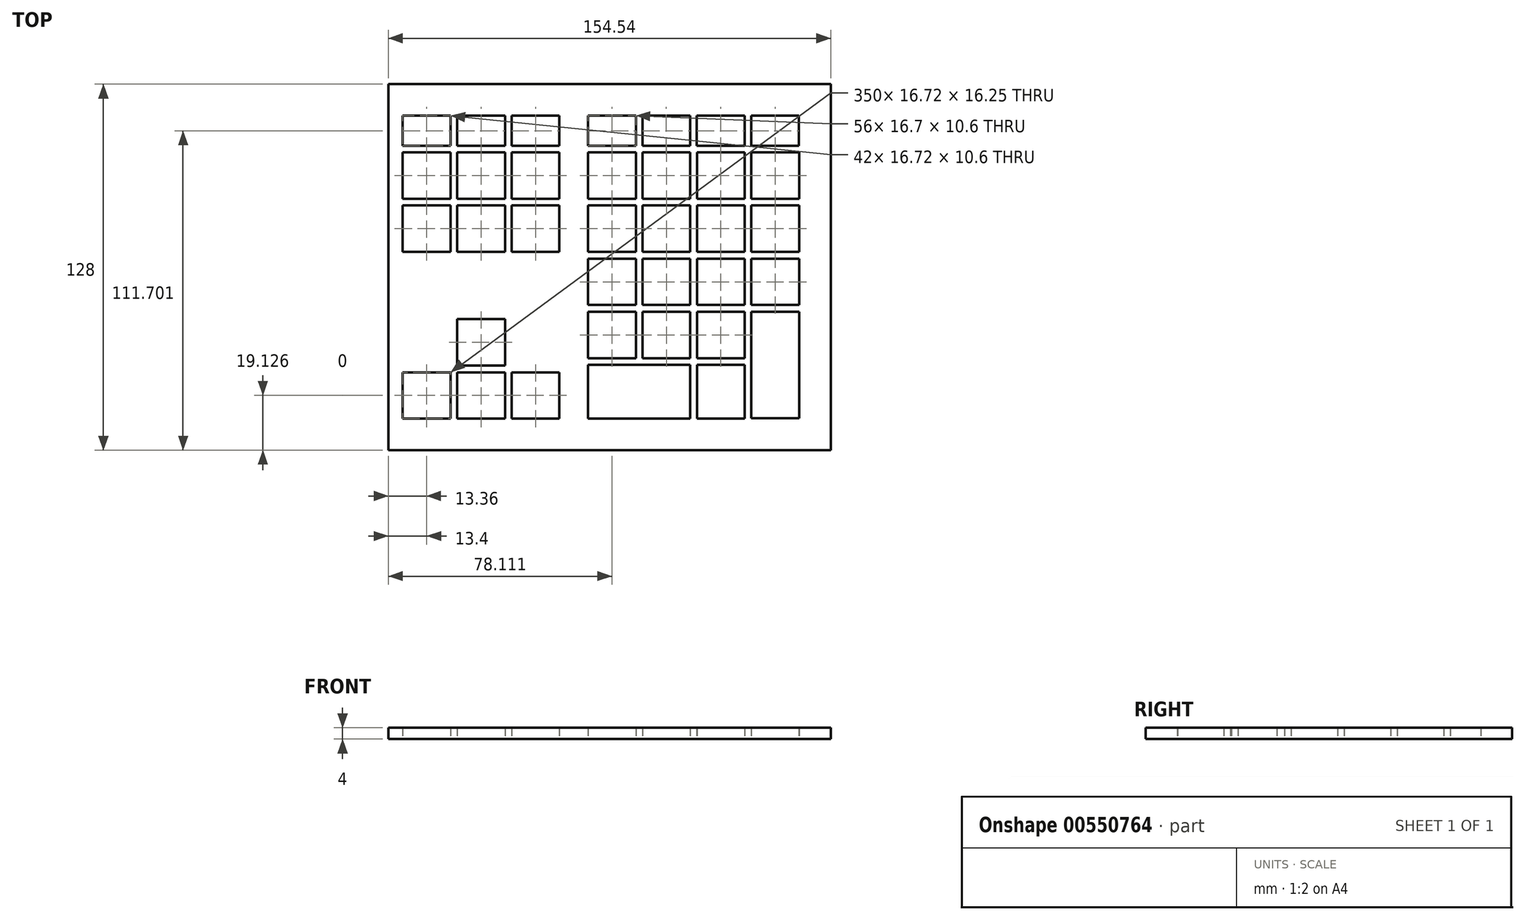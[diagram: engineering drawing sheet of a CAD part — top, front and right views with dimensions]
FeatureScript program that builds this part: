
annotation { "Feature Type Name" : "Feature", "Feature Type Description" : "" }
export const myFeature = defineFeature(function(context is Context, id is Id, definition is map)
    precondition{}
    {
        {
            var Q0;
            Q0=qCreatedBy(makeId("Top.planeOp"),FACE);
            var sketch = newSketch(context, id + "F0", { "sketchPlane" : qUnion([Q0])});
            skLineSegment(sketch, "E0.right", {"start": v(19.3, 78.42) * mm, "end": v(19.3, -35.58) * mm, "construction": true});
            skLineSegment(sketch, "E1.bottom", {"start": v(-123.2, 74.42) * mm, "end": v(-106.49, 74.42) * mm});
            skLineSegment(sketch, "E1.top", {"start": v(-123.2, 63.82) * mm, "end": v(-106.49, 63.82) * mm});
            skLineSegment(sketch, "E1.left", {"start": v(-123.2, 74.42) * mm, "end": v(-123.2, 63.82) * mm});
            skLineSegment(sketch, "E1.right", {"start": v(-106.49, 74.42) * mm, "end": v(-106.49, 63.82) * mm});
            skPoint(sketch, "E1.middle", {"position": v(-114.85, 69.12) * mm});
            skLineSegment(sketch, "E2.1.0.0", {"start": v(-87.49, 74.42) * mm, "end": v(-87.49, 63.82) * mm});
            skLineSegment(sketch, "E2.1.0.1", {"start": v(-104.2, 74.42) * mm, "end": v(-104.2, 63.82) * mm});
            skLineSegment(sketch, "E2.1.0.2", {"start": v(-104.2, 74.42) * mm, "end": v(-87.49, 74.42) * mm});
            skPoint(sketch, "E2.1.0.3", {"position": v(-95.85, 69.12) * mm});
            skLineSegment(sketch, "E2.1.0.4", {"start": v(-104.2, 63.82) * mm, "end": v(-87.49, 63.82) * mm});
            skLineSegment(sketch, "E2.2.0.0", {"start": v(-68.49, 74.42) * mm, "end": v(-68.49, 63.82) * mm});
            skLineSegment(sketch, "E2.2.0.1", {"start": v(-85.2, 74.42) * mm, "end": v(-85.2, 63.82) * mm});
            skLineSegment(sketch, "E2.2.0.2", {"start": v(-85.2, 74.42) * mm, "end": v(-68.49, 74.42) * mm});
            skPoint(sketch, "E2.2.0.3", {"position": v(-76.85, 69.12) * mm});
            skLineSegment(sketch, "E2.2.0.4", {"start": v(-85.2, 63.82) * mm, "end": v(-68.49, 63.82) * mm});
            skLineSegment(sketch, "E3.bottom", {"start": v(-58.49, 74.42) * mm, "end": v(-41.79, 74.42) * mm});
            skLineSegment(sketch, "E3.top", {"start": v(-58.49, 63.82) * mm, "end": v(-41.79, 63.82) * mm});
            skLineSegment(sketch, "E3.left", {"start": v(-58.49, 74.42) * mm, "end": v(-58.49, 63.82) * mm});
            skLineSegment(sketch, "E3.right", {"start": v(-41.79, 74.42) * mm, "end": v(-41.79, 63.82) * mm});
            skPoint(sketch, "E3.middle", {"position": v(-50.14, 69.12) * mm});
            skLineSegment(sketch, "E4.1.0.0", {"start": v(-22.79, 74.42) * mm, "end": v(-22.79, 63.82) * mm});
            skLineSegment(sketch, "E4.1.0.1", {"start": v(-39.49, 74.42) * mm, "end": v(-22.79, 74.42) * mm});
            skLineSegment(sketch, "E4.1.0.2", {"start": v(-39.49, 63.82) * mm, "end": v(-22.79, 63.82) * mm});
            skLineSegment(sketch, "E4.1.0.3", {"start": v(-39.49, 74.42) * mm, "end": v(-39.49, 63.82) * mm});
            skPoint(sketch, "E4.1.0.4", {"position": v(-31.14, 69.12) * mm});
            skLineSegment(sketch, "E4.2.0.0", {"start": v(-3.79, 74.42) * mm, "end": v(-3.79, 63.82) * mm});
            skLineSegment(sketch, "E4.2.0.1", {"start": v(-20.49, 74.42) * mm, "end": v(-3.79, 74.42) * mm});
            skLineSegment(sketch, "E4.2.0.2", {"start": v(-20.49, 63.82) * mm, "end": v(-3.79, 63.82) * mm});
            skLineSegment(sketch, "E4.2.0.3", {"start": v(-20.49, 74.42) * mm, "end": v(-20.49, 63.82) * mm});
            skPoint(sketch, "E4.2.0.4", {"position": v(-12.14, 69.12) * mm});
            skLineSegment(sketch, "E4.3.0.0", {"start": v(15.21, 74.42) * mm, "end": v(15.21, 63.82) * mm});
            skLineSegment(sketch, "E4.3.0.1", {"start": v(-1.49, 74.42) * mm, "end": v(15.21, 74.42) * mm});
            skLineSegment(sketch, "E4.3.0.2", {"start": v(-1.49, 63.82) * mm, "end": v(15.21, 63.82) * mm});
            skLineSegment(sketch, "E4.3.0.3", {"start": v(-1.49, 74.42) * mm, "end": v(-1.49, 63.82) * mm});
            skPoint(sketch, "E4.3.0.4", {"position": v(6.86, 69.12) * mm});
            skLineSegment(sketch, "E5.bottom", {"start": v(-123.25, 61.52) * mm, "end": v(-106.53, 61.52) * mm});
            skLineSegment(sketch, "E5.top", {"start": v(-123.25, 45.27) * mm, "end": v(-106.53, 45.27) * mm});
            skLineSegment(sketch, "E5.left", {"start": v(-123.25, 61.52) * mm, "end": v(-123.25, 45.27) * mm});
            skLineSegment(sketch, "E5.right", {"start": v(-106.53, 61.52) * mm, "end": v(-106.53, 45.27) * mm});
            skPoint(sketch, "E5.middle", {"position": v(-114.89, 53.4) * mm});
            skPoint(sketch, "E6.1.0.0", {"position": v(-95.87, 53.4) * mm});
            skLineSegment(sketch, "E6.1.0.1", {"start": v(-104.23, 45.27) * mm, "end": v(-87.5, 45.27) * mm});
            skLineSegment(sketch, "E6.1.0.2", {"start": v(-87.5, 61.52) * mm, "end": v(-87.5, 45.27) * mm});
            skLineSegment(sketch, "E6.1.0.3", {"start": v(-104.23, 61.52) * mm, "end": v(-87.5, 61.52) * mm});
            skLineSegment(sketch, "E6.1.0.4", {"start": v(-104.23, 61.52) * mm, "end": v(-104.23, 45.27) * mm});
            skPoint(sketch, "E6.2.0.0", {"position": v(-76.85, 53.4) * mm});
            skLineSegment(sketch, "E6.2.0.1", {"start": v(-85.2, 45.27) * mm, "end": v(-68.49, 45.27) * mm});
            skLineSegment(sketch, "E6.2.0.2", {"start": v(-68.49, 61.52) * mm, "end": v(-68.49, 45.27) * mm});
            skLineSegment(sketch, "E6.2.0.3", {"start": v(-85.2, 61.52) * mm, "end": v(-68.49, 61.52) * mm});
            skLineSegment(sketch, "E6.2.0.4", {"start": v(-85.2, 61.52) * mm, "end": v(-85.2, 45.27) * mm});
            skLineSegment(sketch, "E7.bottom", {"start": v(-123.25, 42.97) * mm, "end": v(-106.53, 42.97) * mm});
            skLineSegment(sketch, "E7.top", {"start": v(-123.25, 26.72) * mm, "end": v(-106.53, 26.72) * mm});
            skLineSegment(sketch, "E7.left", {"start": v(-123.25, 42.97) * mm, "end": v(-123.25, 26.72) * mm});
            skLineSegment(sketch, "E7.right", {"start": v(-106.53, 42.97) * mm, "end": v(-106.53, 26.72) * mm});
            skPoint(sketch, "E7.middle", {"position": v(-114.89, 34.85) * mm});
            skLineSegment(sketch, "E8.1.0.0", {"start": v(-104.23, 26.72) * mm, "end": v(-87.5, 26.72) * mm});
            skLineSegment(sketch, "E8.1.0.1", {"start": v(-104.23, 42.97) * mm, "end": v(-87.5, 42.97) * mm});
            skLineSegment(sketch, "E8.1.0.2", {"start": v(-104.23, 42.97) * mm, "end": v(-104.23, 26.72) * mm});
            skPoint(sketch, "E8.1.0.3", {"position": v(-95.87, 34.85) * mm});
            skLineSegment(sketch, "E8.1.0.4", {"start": v(-87.5, 42.97) * mm, "end": v(-87.5, 26.72) * mm});
            skLineSegment(sketch, "E8.2.0.0", {"start": v(-85.2, 26.72) * mm, "end": v(-68.49, 26.72) * mm});
            skLineSegment(sketch, "E8.2.0.1", {"start": v(-85.2, 42.97) * mm, "end": v(-68.49, 42.97) * mm});
            skLineSegment(sketch, "E8.2.0.2", {"start": v(-85.2, 42.97) * mm, "end": v(-85.2, 26.72) * mm});
            skPoint(sketch, "E8.2.0.3", {"position": v(-76.85, 34.85) * mm});
            skLineSegment(sketch, "E8.2.0.4", {"start": v(-68.49, 42.97) * mm, "end": v(-68.49, 26.72) * mm});
            skPoint(sketch, "E9.1.0.0", {"position": v(-50.13, 53.4) * mm});
            skLineSegment(sketch, "E9.1.0.1", {"start": v(-58.49, 61.52) * mm, "end": v(-41.77, 61.52) * mm});
            skLineSegment(sketch, "E9.1.0.3", {"start": v(-41.77, 61.52) * mm, "end": v(-41.77, 45.27) * mm});
            skLineSegment(sketch, "E9.1.0.4", {"start": v(-58.49, 45.27) * mm, "end": v(-41.77, 45.27) * mm});
            skLineSegment(sketch, "E9.1.0.7", {"start": v(-58.49, 61.52) * mm, "end": v(-58.49, 45.27) * mm});
            skLineSegment(sketch, "E10.0.1.0", {"start": v(-58.49, 42.97) * mm, "end": v(-58.49, 26.72) * mm});
            skPoint(sketch, "E10.0.1.1", {"position": v(-50.13, 34.85) * mm});
            skLineSegment(sketch, "E10.0.1.2", {"start": v(-58.49, 42.97) * mm, "end": v(-41.77, 42.97) * mm});
            skLineSegment(sketch, "E10.0.1.3", {"start": v(-41.77, 42.97) * mm, "end": v(-41.77, 26.72) * mm});
            skLineSegment(sketch, "E10.0.1.4", {"start": v(-58.49, 26.72) * mm, "end": v(-41.77, 26.72) * mm});
            skLineSegment(sketch, "E10.0.2.0", {"start": v(-58.49, 24.42) * mm, "end": v(-58.49, 8.17) * mm});
            skPoint(sketch, "E10.0.2.1", {"position": v(-50.13, 16.3) * mm});
            skLineSegment(sketch, "E10.0.2.2", {"start": v(-58.49, 24.42) * mm, "end": v(-41.77, 24.42) * mm});
            skLineSegment(sketch, "E10.0.2.3", {"start": v(-41.77, 24.42) * mm, "end": v(-41.77, 8.17) * mm});
            skLineSegment(sketch, "E10.0.2.4", {"start": v(-58.49, 8.17) * mm, "end": v(-41.77, 8.17) * mm});
            skLineSegment(sketch, "E10.0.3.0", {"start": v(-58.49, 5.87) * mm, "end": v(-58.49, -10.38) * mm});
            skPoint(sketch, "E10.0.3.1", {"position": v(-50.13, -2.25) * mm});
            skLineSegment(sketch, "E10.0.3.2", {"start": v(-58.49, 5.87) * mm, "end": v(-41.77, 5.87) * mm});
            skLineSegment(sketch, "E10.0.3.3", {"start": v(-41.77, 5.87) * mm, "end": v(-41.77, -10.38) * mm});
            skLineSegment(sketch, "E10.0.3.4", {"start": v(-58.49, -10.38) * mm, "end": v(-41.77, -10.38) * mm});
            skLineSegment(sketch, "E10.1.0.0", {"start": v(-39.47, 61.52) * mm, "end": v(-39.47, 45.27) * mm});
            skPoint(sketch, "E10.1.0.1", {"position": v(-31.1, 53.4) * mm});
            skLineSegment(sketch, "E10.1.0.2", {"start": v(-39.47, 61.52) * mm, "end": v(-22.75, 61.52) * mm});
            skLineSegment(sketch, "E10.1.0.3", {"start": v(-22.75, 61.52) * mm, "end": v(-22.75, 45.27) * mm});
            skLineSegment(sketch, "E10.1.0.4", {"start": v(-39.47, 45.27) * mm, "end": v(-22.75, 45.27) * mm});
            skLineSegment(sketch, "E10.1.1.0", {"start": v(-39.47, 42.97) * mm, "end": v(-39.47, 26.72) * mm});
            skPoint(sketch, "E10.1.1.1", {"position": v(-31.1, 34.85) * mm});
            skLineSegment(sketch, "E10.1.1.2", {"start": v(-39.47, 42.97) * mm, "end": v(-22.75, 42.97) * mm});
            skLineSegment(sketch, "E10.1.1.3", {"start": v(-22.75, 42.97) * mm, "end": v(-22.75, 26.72) * mm});
            skLineSegment(sketch, "E10.1.1.4", {"start": v(-39.47, 26.72) * mm, "end": v(-22.75, 26.72) * mm});
            skLineSegment(sketch, "E10.1.2.0", {"start": v(-39.47, 24.42) * mm, "end": v(-39.47, 8.17) * mm});
            skPoint(sketch, "E10.1.2.1", {"position": v(-31.1, 16.3) * mm});
            skLineSegment(sketch, "E10.1.2.2", {"start": v(-39.47, 24.42) * mm, "end": v(-22.75, 24.42) * mm});
            skLineSegment(sketch, "E10.1.2.3", {"start": v(-22.75, 24.42) * mm, "end": v(-22.75, 8.17) * mm});
            skLineSegment(sketch, "E10.1.2.4", {"start": v(-39.47, 8.17) * mm, "end": v(-22.75, 8.17) * mm});
            skLineSegment(sketch, "E10.1.3.0", {"start": v(-39.47, 5.87) * mm, "end": v(-39.47, -10.38) * mm});
            skPoint(sketch, "E10.1.3.1", {"position": v(-31.1, -2.25) * mm});
            skLineSegment(sketch, "E10.1.3.2", {"start": v(-39.47, 5.87) * mm, "end": v(-22.75, 5.87) * mm});
            skLineSegment(sketch, "E10.1.3.3", {"start": v(-22.75, 5.87) * mm, "end": v(-22.75, -10.38) * mm});
            skLineSegment(sketch, "E10.1.3.4", {"start": v(-39.47, -10.38) * mm, "end": v(-22.75, -10.38) * mm});
            skLineSegment(sketch, "E10.2.0.0", {"start": v(-20.45, 61.52) * mm, "end": v(-20.45, 45.27) * mm});
            skPoint(sketch, "E10.2.0.1", {"position": v(-12.09, 53.4) * mm});
            skLineSegment(sketch, "E10.2.0.2", {"start": v(-20.45, 61.52) * mm, "end": v(-3.73, 61.52) * mm});
            skLineSegment(sketch, "E10.2.0.3", {"start": v(-3.73, 61.52) * mm, "end": v(-3.73, 45.27) * mm});
            skLineSegment(sketch, "E10.2.0.4", {"start": v(-20.45, 45.27) * mm, "end": v(-3.73, 45.27) * mm});
            skLineSegment(sketch, "E10.2.1.0", {"start": v(-20.45, 42.97) * mm, "end": v(-20.45, 26.72) * mm});
            skPoint(sketch, "E10.2.1.1", {"position": v(-12.09, 34.85) * mm});
            skLineSegment(sketch, "E10.2.1.2", {"start": v(-20.45, 42.97) * mm, "end": v(-3.73, 42.97) * mm});
            skLineSegment(sketch, "E10.2.1.3", {"start": v(-3.73, 42.97) * mm, "end": v(-3.73, 26.72) * mm});
            skLineSegment(sketch, "E10.2.1.4", {"start": v(-20.45, 26.72) * mm, "end": v(-3.73, 26.72) * mm});
            skLineSegment(sketch, "E10.2.2.0", {"start": v(-20.45, 24.42) * mm, "end": v(-20.45, 8.17) * mm});
            skPoint(sketch, "E10.2.2.1", {"position": v(-12.09, 16.3) * mm});
            skLineSegment(sketch, "E10.2.2.2", {"start": v(-20.45, 24.42) * mm, "end": v(-3.73, 24.42) * mm});
            skLineSegment(sketch, "E10.2.2.3", {"start": v(-3.73, 24.42) * mm, "end": v(-3.73, 8.17) * mm});
            skLineSegment(sketch, "E10.2.2.4", {"start": v(-20.45, 8.17) * mm, "end": v(-3.73, 8.17) * mm});
            skLineSegment(sketch, "E10.2.3.0", {"start": v(-20.45, 5.87) * mm, "end": v(-20.45, -10.38) * mm});
            skPoint(sketch, "E10.2.3.1", {"position": v(-12.09, -2.25) * mm});
            skLineSegment(sketch, "E10.2.3.2", {"start": v(-20.45, 5.87) * mm, "end": v(-3.73, 5.87) * mm});
            skLineSegment(sketch, "E10.2.3.3", {"start": v(-3.73, 5.87) * mm, "end": v(-3.73, -10.38) * mm});
            skLineSegment(sketch, "E10.2.3.4", {"start": v(-20.45, -10.38) * mm, "end": v(-3.73, -10.38) * mm});
            skLineSegment(sketch, "E10.3.0.0", {"start": v(-1.43, 61.52) * mm, "end": v(-1.43, 45.27) * mm});
            skPoint(sketch, "E10.3.0.1", {"position": v(6.93, 53.4) * mm});
            skLineSegment(sketch, "E10.3.0.2", {"start": v(-1.43, 61.52) * mm, "end": v(15.3, 61.52) * mm});
            skLineSegment(sketch, "E10.3.0.3", {"start": v(15.3, 61.52) * mm, "end": v(15.3, 45.27) * mm});
            skLineSegment(sketch, "E10.3.0.4", {"start": v(-1.43, 45.27) * mm, "end": v(15.3, 45.27) * mm});
            skLineSegment(sketch, "E10.3.1.0", {"start": v(-1.43, 42.97) * mm, "end": v(-1.43, 26.72) * mm});
            skPoint(sketch, "E10.3.1.1", {"position": v(6.93, 34.85) * mm});
            skLineSegment(sketch, "E10.3.1.2", {"start": v(-1.43, 42.97) * mm, "end": v(15.3, 42.97) * mm});
            skLineSegment(sketch, "E10.3.1.3", {"start": v(15.3, 42.97) * mm, "end": v(15.3, 26.72) * mm});
            skLineSegment(sketch, "E10.3.1.4", {"start": v(-1.43, 26.72) * mm, "end": v(15.3, 26.72) * mm});
            skLineSegment(sketch, "E10.3.2.0", {"start": v(-1.43, 24.42) * mm, "end": v(-1.43, 8.17) * mm});
            skPoint(sketch, "E10.3.2.1", {"position": v(6.93, 16.3) * mm});
            skLineSegment(sketch, "E10.3.2.2", {"start": v(-1.43, 24.42) * mm, "end": v(15.3, 24.42) * mm});
            skLineSegment(sketch, "E10.3.2.3", {"start": v(15.3, 24.42) * mm, "end": v(15.3, 8.17) * mm});
            skLineSegment(sketch, "E10.3.2.4", {"start": v(-1.43, 8.17) * mm, "end": v(15.3, 8.17) * mm});
            skLineSegment(sketch, "E10.3.3.0", {"start": v(-1.43, 5.87) * mm, "end": v(-1.43, -31.43) * mm});
            skPoint(sketch, "E10.3.3.1", {"position": v(6.93, -12.78) * mm});
            skLineSegment(sketch, "E10.3.3.2", {"start": v(-1.43, 5.87) * mm, "end": v(15.3, 5.87) * mm});
            skLineSegment(sketch, "E10.3.3.3", {"start": v(15.3, 5.87) * mm, "end": v(15.3, -31.43) * mm});
            skLineSegment(sketch, "E10.3.3.4", {"start": v(-1.43, -31.43) * mm, "end": v(15.3, -31.43) * mm});
            skLineSegment(sketch, "E11.bottom", {"start": v(-20.45, -12.68) * mm, "end": v(-3.73, -12.68) * mm});
            skLineSegment(sketch, "E11.top", {"start": v(-20.45, -31.49) * mm, "end": v(-3.73, -31.49) * mm});
            skLineSegment(sketch, "E11.left", {"start": v(-20.45, -12.68) * mm, "end": v(-20.45, -31.49) * mm});
            skLineSegment(sketch, "E11.right", {"start": v(-3.73, -12.68) * mm, "end": v(-3.73, -31.49) * mm});
            skPoint(sketch, "E11.middle", {"position": v(-12.09, -22.08) * mm});
            skLineSegment(sketch, "E12.bottom", {"start": v(-58.49, -12.68) * mm, "end": v(-22.75, -12.68) * mm});
            skLineSegment(sketch, "E12.top", {"start": v(-58.49, -31.49) * mm, "end": v(-22.75, -31.49) * mm});
            skLineSegment(sketch, "E12.left", {"start": v(-58.49, -12.68) * mm, "end": v(-58.49, -31.49) * mm});
            skLineSegment(sketch, "E12.right", {"start": v(-22.75, -12.68) * mm, "end": v(-22.75, -31.49) * mm});
            skPoint(sketch, "E12.middle", {"position": v(-40.62, -22.08) * mm});
            skLineSegment(sketch, "E13.bottom", {"start": v(-85.2, -15.33) * mm, "end": v(-68.49, -15.33) * mm});
            skLineSegment(sketch, "E13.top", {"start": v(-85.2, -31.58) * mm, "end": v(-68.49, -31.58) * mm});
            skLineSegment(sketch, "E13.left", {"start": v(-85.2, -15.33) * mm, "end": v(-85.2, -31.58) * mm});
            skLineSegment(sketch, "E13.right", {"start": v(-68.49, -15.33) * mm, "end": v(-68.49, -31.58) * mm});
            skPoint(sketch, "E13.middle", {"position": v(-76.85, -23.45) * mm});
            skPoint(sketch, "E14.1.0.0", {"position": v(-95.87, -23.45) * mm});
            skLineSegment(sketch, "E14.1.0.1", {"start": v(-104.23, -31.58) * mm, "end": v(-87.5, -31.58) * mm});
            skLineSegment(sketch, "E14.1.0.2", {"start": v(-104.23, -15.33) * mm, "end": v(-87.5, -15.33) * mm});
            skLineSegment(sketch, "E14.1.0.3", {"start": v(-87.5, -15.33) * mm, "end": v(-87.5, -31.58) * mm});
            skLineSegment(sketch, "E14.1.0.4", {"start": v(-104.23, -15.33) * mm, "end": v(-104.23, -31.58) * mm});
            skPoint(sketch, "E14.2.0.0", {"position": v(-114.89, -23.45) * mm});
            skLineSegment(sketch, "E14.2.0.1", {"start": v(-123.25, -31.58) * mm, "end": v(-106.53, -31.58) * mm});
            skLineSegment(sketch, "E14.2.0.2", {"start": v(-123.25, -15.33) * mm, "end": v(-106.53, -15.33) * mm});
            skLineSegment(sketch, "E14.2.0.3", {"start": v(-106.53, -15.33) * mm, "end": v(-106.53, -31.58) * mm});
            skLineSegment(sketch, "E14.2.0.4", {"start": v(-123.25, -15.33) * mm, "end": v(-123.25, -31.58) * mm});
            skLineSegment(sketch, "E15.0.1.0", {"start": v(-104.23, 3.22) * mm, "end": v(-87.5, 3.22) * mm});
            skLineSegment(sketch, "E15.0.1.1", {"start": v(-104.23, 3.22) * mm, "end": v(-104.23, -13.03) * mm});
            skLineSegment(sketch, "E15.0.1.2", {"start": v(-87.5, 3.22) * mm, "end": v(-87.5, -13.03) * mm});
            skPoint(sketch, "E15.0.1.3", {"position": v(-95.87, -4.9) * mm});
            skLineSegment(sketch, "E15.0.1.4", {"start": v(-104.23, -13.03) * mm, "end": v(-87.5, -13.03) * mm});
            skLineSegment(sketch, "E16.right", {"start": v(26.3, 85.42) * mm, "end": v(26.3, -42.58) * mm});
            skLineSegment(sketch, "E17", {"start": v(-128.25, 85.42) * mm, "end": v(-128.25, 78.42) * mm});
            skLineSegment(sketch, "E18", {"start": v(-128.25, 85.42) * mm, "end": v(26.3, 85.42) * mm});
            skLineSegment(sketch, "E19", {"start": v(-128.25, -42.58) * mm, "end": v(26.3, -42.58) * mm});
            skLineSegment(sketch, "E20", {"start": v(-128.25, -35.58) * mm, "end": v(-128.25, -42.58) * mm});
            skLineSegment(sketch, "E21", {"start": v(-128.25, 78.42) * mm, "end": v(-128.25, -35.58) * mm});
            skSolve(sketch);
        }
        {
            var Q0;
            Q0=makeQuery(id+"F0.imprint","IMPRINT",FACE,{"disambiguationData":[TD([[makeQuery(id+"F0.imprint","IMPRINT",EDGE,{"derivedFrom":sQuery(id+"F0.wireOp",EDGE,"E1.bottom")}),1.0]])]});
            extrude(context, id + "F1", {"entities" : qUnion([Q0]), "depth" : 4 * mm, "offsetDistance" : 25 * mm});
        }
    });
